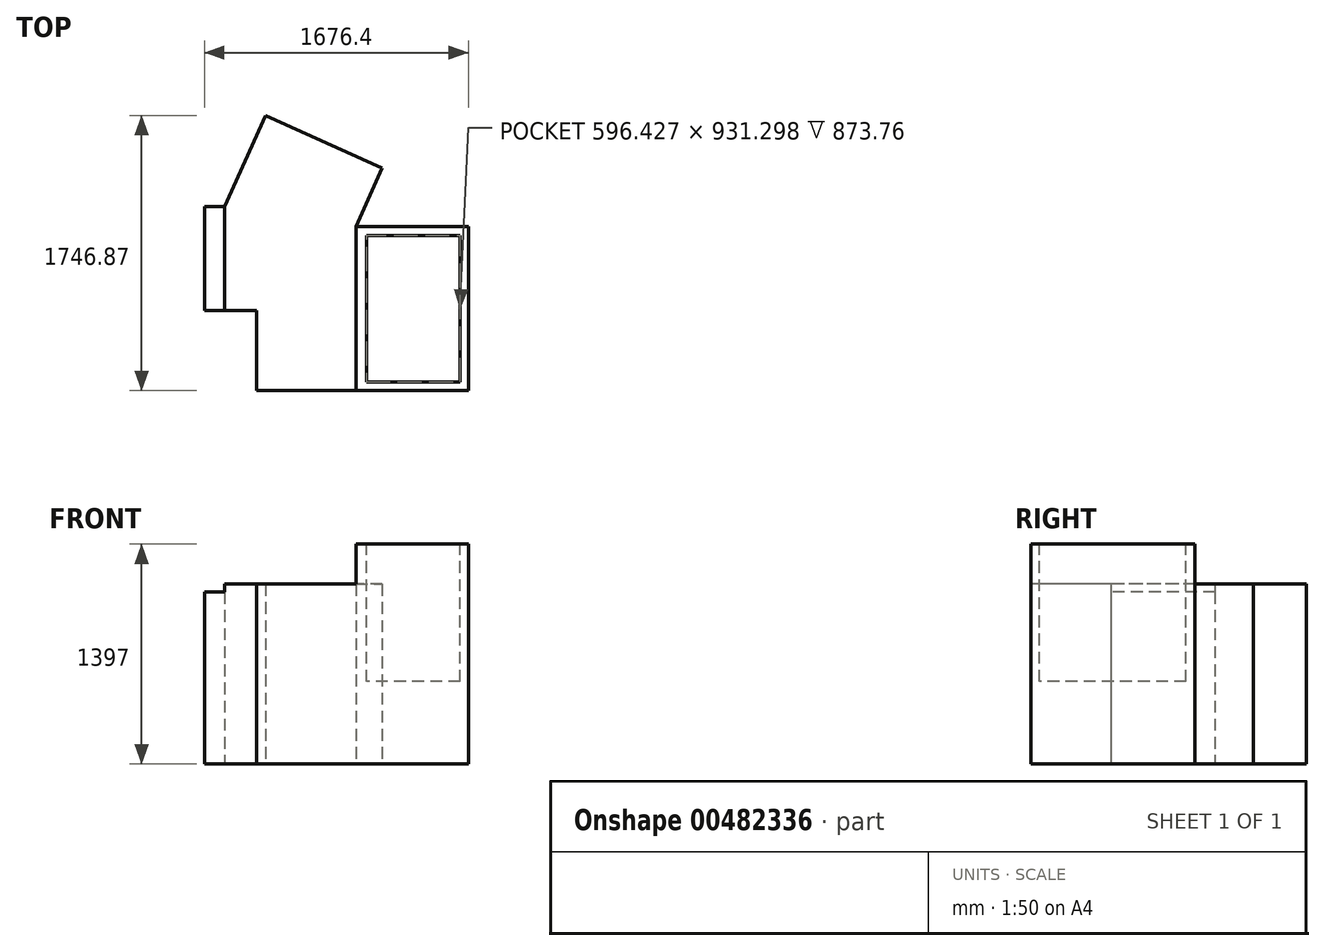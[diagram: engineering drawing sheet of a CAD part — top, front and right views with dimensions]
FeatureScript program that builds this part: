
annotation { "Feature Type Name" : "Feature", "Feature Type Description" : "" }
export const myFeature = defineFeature(function(context is Context, id is Id, definition is map)
    precondition{}
    {
        {
            var Q0;
            Q0=qCreatedBy(makeId("Top.planeOp"),FACE);
            var sketch = newSketch(context, id + "F0", { "sketchPlane" : qUnion([Q0])});
            skLineSegment(sketch, "E0", {"start": v(0, 0) * mm, "end": v(-203.2, 0) * mm});
            skLineSegment(sketch, "E1", {"start": v(-203.2, 0) * mm, "end": v(-330.2, 0) * mm});
            skLineSegment(sketch, "E2", {"start": v(-330.2, 0) * mm, "end": v(-330.2, 660.4) * mm});
            skLineSegment(sketch, "E3", {"start": v(-330.2, 660.4) * mm, "end": v(-203.2, 660.4) * mm});
            skLineSegment(sketch, "E4", {"start": v(-203.2, 660.4) * mm, "end": v(-203.2, 0) * mm});
            skLineSegment(sketch, "E5", {"start": v(0, 0) * mm, "end": v(0, -508) * mm});
            skLineSegment(sketch, "E6", {"start": v(0, -508) * mm, "end": v(1346.2, -508) * mm});
            skLineSegment(sketch, "E7", {"start": v(1346.2, -508) * mm, "end": v(1346.2, 533.4) * mm});
            skLineSegment(sketch, "E8", {"start": v(1346.2, 533.4) * mm, "end": v(631.53, 533.4) * mm});
            skLineSegment(sketch, "E9", {"start": v(631.53, 533.4) * mm, "end": v(799.15, 903.62) * mm});
            skLineSegment(sketch, "E10", {"start": v(799.15, 903.62) * mm, "end": v(58.71, 1238.87) * mm});
            skLineSegment(sketch, "E11", {"start": v(58.71, 1238.87) * mm, "end": v(-203.2, 660.4) * mm});
            skLineSegment(sketch, "E12", {"start": v(631.53, 533.4) * mm, "end": v(631.53, -508) * mm});
            skSolve(sketch);
        }
        {
            var Q0;
            {var subQ0=sQuery(id+"F0.wireOp",EDGE,"E7");Q0=makeQuery(id+"F0.imprint","IMPRINT",FACE,{"disambiguationData":[TD([[makeQuery(id+"F0.imprint","IMPRINT",EDGE,{"derivedFrom":subQ0}),1.0]])]});}
            extrude(context, id + "F1", {"entities" : qUnion([Q0]), "depth" : 1397 * mm, "offsetDistance" : 25.4 * mm});
        }
        {
            var Q0;
            Q0=makeQuery(id+"F0.imprint","IMPRINT",FACE,{"disambiguationData":[TD([[makeQuery(id+"F0.imprint","IMPRINT",EDGE,{"derivedFrom":sQuery(id+"F0.wireOp",EDGE,"E0")}),-1.0]])]});
            extrude(context, id + "F2", {"entities" : qUnion([Q0]), "operationType" : NewBodyOperationType.ADD, "depth" : 1143 * mm, "offsetDistance" : 25.4 * mm});
        }
        {
            var Q0;
            Q0=makeQuery(id+"F0.imprint","IMPRINT",FACE,{"disambiguationData":[TD([[makeQuery(id+"F0.imprint","IMPRINT",EDGE,{"derivedFrom":sQuery(id+"F0.wireOp",EDGE,"E1")}),-1.0]])]});
            extrude(context, id + "F3", {"entities" : qUnion([Q0]), "operationType" : NewBodyOperationType.ADD, "depth" : 1092.2 * mm, "offsetDistance" : 25.4 * mm});
        }
        {
            var Q0;
            Q0=makeQuery(id+"F1.opExtrude","CAP_FACE",FACE,{"disambiguationData":[OSD([sQuery(id+"F0.wireOp",EDGE,"E6"),sQuery(id+"F0.wireOp",EDGE,"E7"),sQuery(id+"F0.wireOp",EDGE,"E8"),sQuery(id+"F0.wireOp",EDGE,"E12")])],"isStart":false});
            var sketch = newSketch(context, id + "F4", { "sketchPlane" : qUnion([Q0])});
            skLineSegment(sketch, "E13.bottom", {"start": v(1294.34, 476.2) * mm, "end": v(697.91, 476.2) * mm});
            skLineSegment(sketch, "E13.top", {"start": v(1294.34, -455.1) * mm, "end": v(697.91, -455.1) * mm});
            skLineSegment(sketch, "E13.left", {"start": v(1294.34, 476.2) * mm, "end": v(1294.34, -455.1) * mm});
            skLineSegment(sketch, "E13.right", {"start": v(697.91, 476.2) * mm, "end": v(697.91, -455.1) * mm});
            skSolve(sketch);
        }
        {
            var Q0;
            Q0 = qSketchRegion(id + "F4", true);
            extrude(context, id + "F5", {"entities" : qUnion([Q0]), "operationType" : NewBodyOperationType.REMOVE, "oppositeDirection" : true, "depth" : 873.76 * mm, "offsetDistance" : 25.4 * mm});
        }
    });
